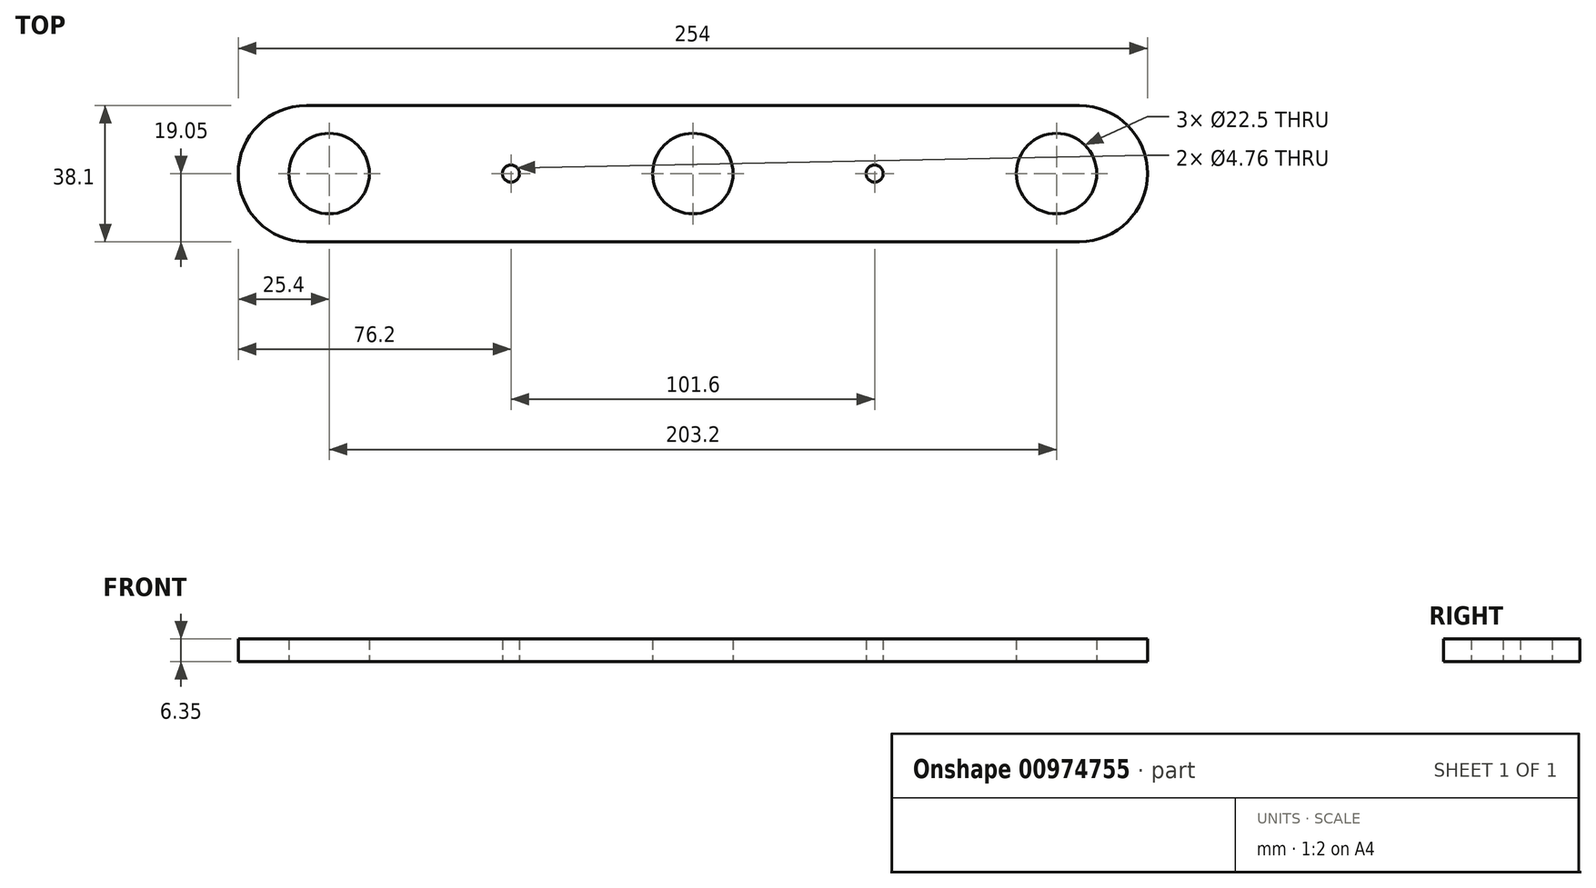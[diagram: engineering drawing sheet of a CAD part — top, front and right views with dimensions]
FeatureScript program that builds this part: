
annotation { "Feature Type Name" : "Feature", "Feature Type Description" : "" }
export const myFeature = defineFeature(function(context is Context, id is Id, definition is map)
    precondition{}
    {
        {
            var Q0;
            Q0=qCreatedBy(makeId("Top.planeOp"),FACE);
            var sketch = newSketch(context, id + "F0", { "sketchPlane" : qUnion([Q0])});
            skArc(sketch, "E0", {"start": v(-57.15, 19.05) * mm, "mid": v(-76.2, 0) * mm, "end": v(-57.15, -19.05) * mm});
            skLineSegment(sketch, "E1", {"start": v(-57.15, 19.05) * mm, "end": v(158.75, 19.05) * mm});
            skLineSegment(sketch, "E2", {"start": v(-57.15, -19.05) * mm, "end": v(158.75, -19.05) * mm});
            skCircle(sketch, "E3", {"center": v(-50.8, 0) * mm, "radius": 11.25 * mm});
            skCircle(sketch, "E4", {"center": v(50.8, 0) * mm, "radius": 11.25 * mm});
            skPoint(sketch, "E5", {"position": v(0, 0) * mm});
            skCircle(sketch, "E6", {"center": v(152.4, 0) * mm, "radius": 11.25 * mm});
            skPoint(sketch, "E7", {"position": v(158.75, 0) * mm});
            skArc(sketch, "E8", {"start": v(158.75, 19.05) * mm, "mid": v(177.8, 0) * mm, "end": v(158.75, -19.05) * mm});
            skPoint(sketch, "E9", {"position": v(101.6, 0) * mm});
            skSolve(sketch);
        }
        {
            var Q0;
            Q0=makeQuery(id+"F0.imprint","IMPRINT",FACE,{"disambiguationData":[TD([[makeQuery(id+"F0.imprint","IMPRINT",EDGE,{"derivedFrom":sQuery(id+"F0.wireOp",EDGE,"E0")}),1.0]])]});
            var sketch = newSketch(context, id + "F1", { "sketchPlane" : qUnion([Q0])});
            skCircle(sketch, "E10", {"center": v(0, 0) * mm, "radius": 2.38 * mm});
            skCircle(sketch, "E11", {"center": v(101.6, 0) * mm, "radius": 2.38 * mm});
            skSolve(sketch);
        }
        {
            var Q0;
            Q0 = qSketchRegion(id + "F0", true);
            extrude(context, id + "F2", {"entities" : qUnion([Q0]), "depth" : 6.35 * mm, "offsetDistance" : 25.4 * mm});
        }
        {
            var Q0;
            Q0 = qSketchRegion(id + "F1", true);
            extrude(context, id + "F3", {"entities" : qUnion([Q0]), "operationType" : NewBodyOperationType.REMOVE, "depth" : 25.4 * mm, "offsetDistance" : 25.4 * mm});
        }
    });
